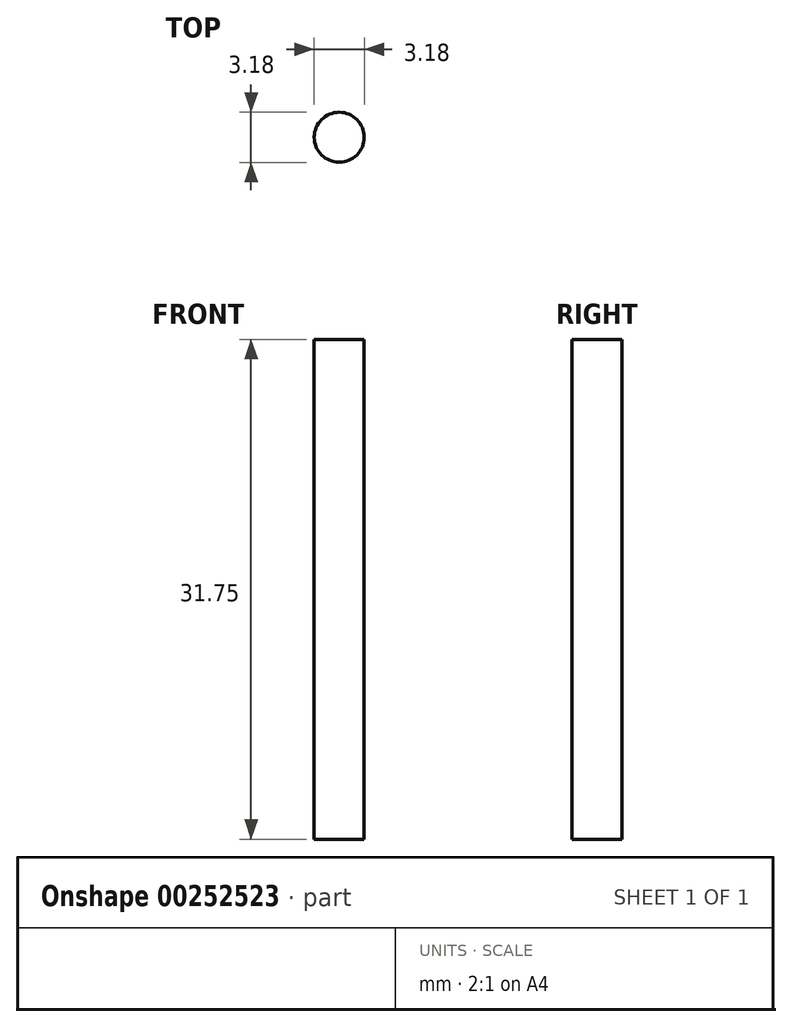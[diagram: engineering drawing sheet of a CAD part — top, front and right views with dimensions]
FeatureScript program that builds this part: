
annotation { "Feature Type Name" : "Feature", "Feature Type Description" : "" }
export const myFeature = defineFeature(function(context is Context, id is Id, definition is map)
    precondition{}
    {
        {
            var Q0;
            Q0=qCreatedBy(makeId("Top.planeOp"),FACE);
            var sketch = newSketch(context, id + "F0", { "sketchPlane" : qUnion([Q0])});
            skCircle(sketch, "E0", {"center": v(0, 0) * mm, "radius": 1.59 * mm});
            skSolve(sketch);
        }
        {
            var Q0;
            Q0=makeQuery(id+"F0.imprint","IMPRINT",FACE,{"disambiguationData":[TD([[makeQuery(id+"F0.imprint","IMPRINT",EDGE,{"derivedFrom":sQuery(id+"F0.wireOp",EDGE,"E0")}),1.0]])]});
            extrude(context, id + "F1", {"entities" : qUnion([Q0]), "depth" : 31.75 * mm});
        }
    });
